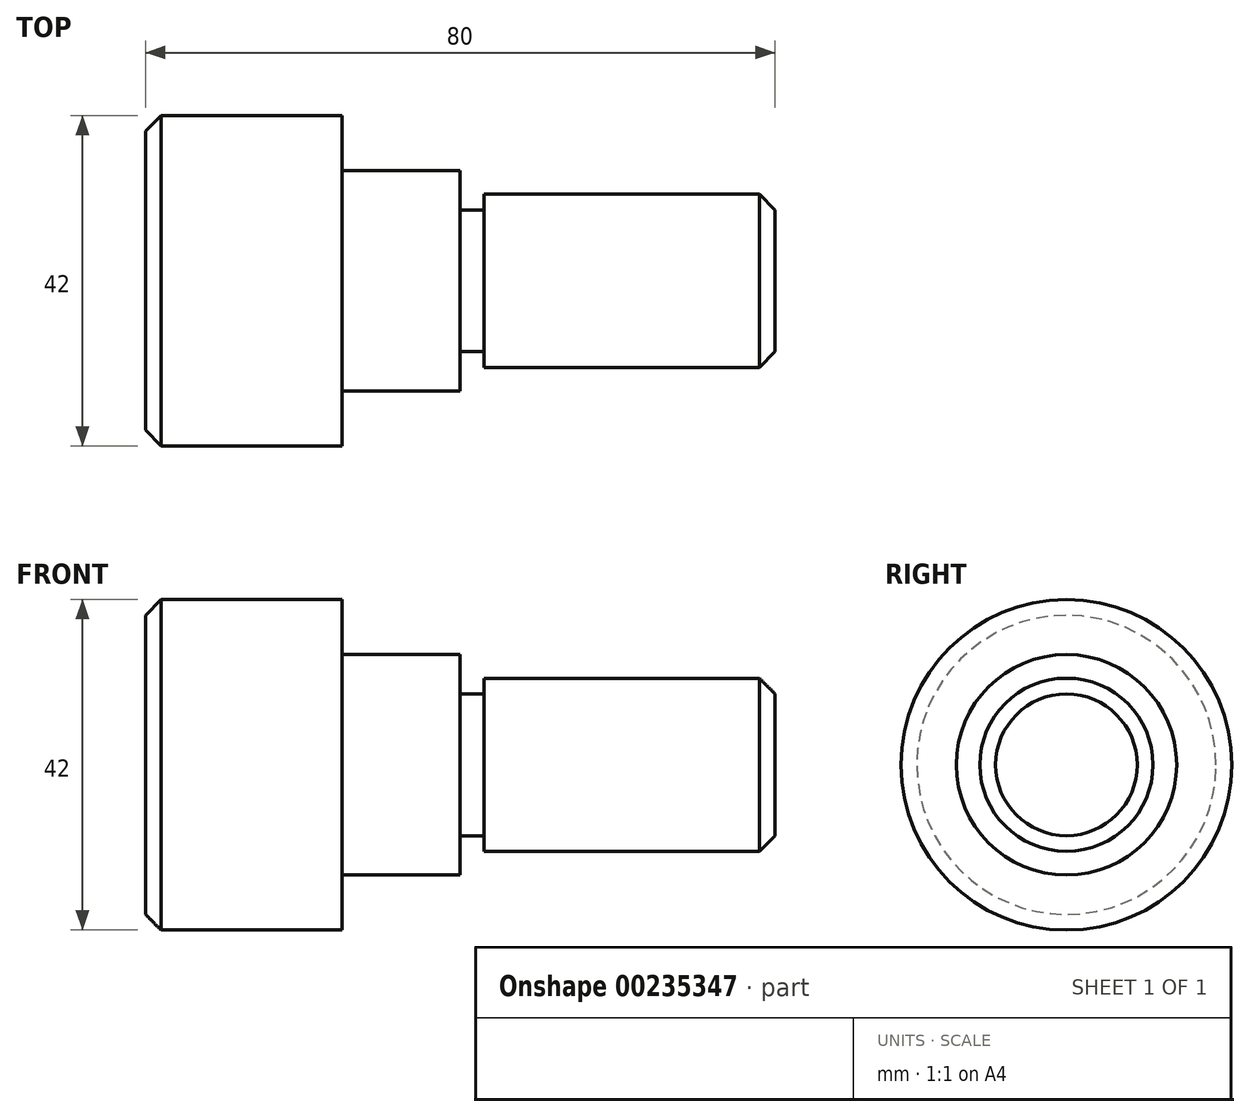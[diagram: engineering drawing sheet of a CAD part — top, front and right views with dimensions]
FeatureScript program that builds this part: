
annotation { "Feature Type Name" : "Feature", "Feature Type Description" : "" }
export const myFeature = defineFeature(function(context is Context, id is Id, definition is map)
    precondition{}
    {
        {
            var Q0;
            Q0=qCreatedBy(makeId("Front.planeOp"),FACE);
            var sketch = newSketch(context, id + "F0", { "sketchPlane" : qUnion([Q0])});
            skLineSegment(sketch, "E0", {"start": v(-80, -21) * mm, "end": v(-55, -21) * mm});
            skLineSegment(sketch, "E1", {"start": v(-55, -21) * mm, "end": v(-55, -14) * mm});
            skLineSegment(sketch, "E2", {"start": v(-55, -14) * mm, "end": v(-40, -14) * mm});
            skLineSegment(sketch, "E3", {"start": v(-40, -14) * mm, "end": v(-40, -9) * mm});
            skLineSegment(sketch, "E4", {"start": v(-40, -9) * mm, "end": v(-37, -9) * mm});
            skLineSegment(sketch, "E5", {"start": v(-37, -9) * mm, "end": v(-37, -11) * mm});
            skLineSegment(sketch, "E6", {"start": v(-37, -11) * mm, "end": v(0, -11) * mm});
            skLineSegment(sketch, "E7", {"start": v(0, -11) * mm, "end": v(0, 0) * mm});
            skLineSegment(sketch, "E8", {"start": v(0, 0) * mm, "end": v(-80, 0) * mm});
            skLineSegment(sketch, "E9", {"start": v(-80, 0) * mm, "end": v(-80, -21) * mm});
            skSolve(sketch);
        }
        {
            var Q0;
            Q0=makeQuery(id+"F0.imprint","IMPRINT",FACE,{"disambiguationData":[TD([[makeQuery(id+"F0.imprint","IMPRINT",EDGE,{"derivedFrom":sQuery(id+"F0.wireOp",EDGE,"E0")}),1.0]])]});
            var Q1;
            Q1=sQuery(id+"F0.wireOp",EDGE,"E8");
            revolve(context, id + "F1", {"entities" : qUnion([Q0]), "axis" : qUnion([Q1]), "revolveType" : RevolveType.FULL});
        }
        {
            var Q0;
            Q0=makeQuery(id+"F1.opRevolve","SWEPT_FACE",FACE,{"disambiguationData":[OSD([sQuery(id+"F0.wireOp",EDGE,"E7")])]});
            var Q1;
            Q1=makeQuery(id+"F1.opRevolve","SWEPT_FACE",FACE,{"disambiguationData":[OSD([sQuery(id+"F0.wireOp",EDGE,"E9")])]});
            chamfer(context, id + "F2", {"entities" : qUnion([Q0, Q1]), "chamferType" : ChamferType.OFFSET_ANGLE, "width" : 2 * mm, "oppositeDirection" : false, "angle" : 45 * degree, "tangentPropagation" : true});
        }
    });
